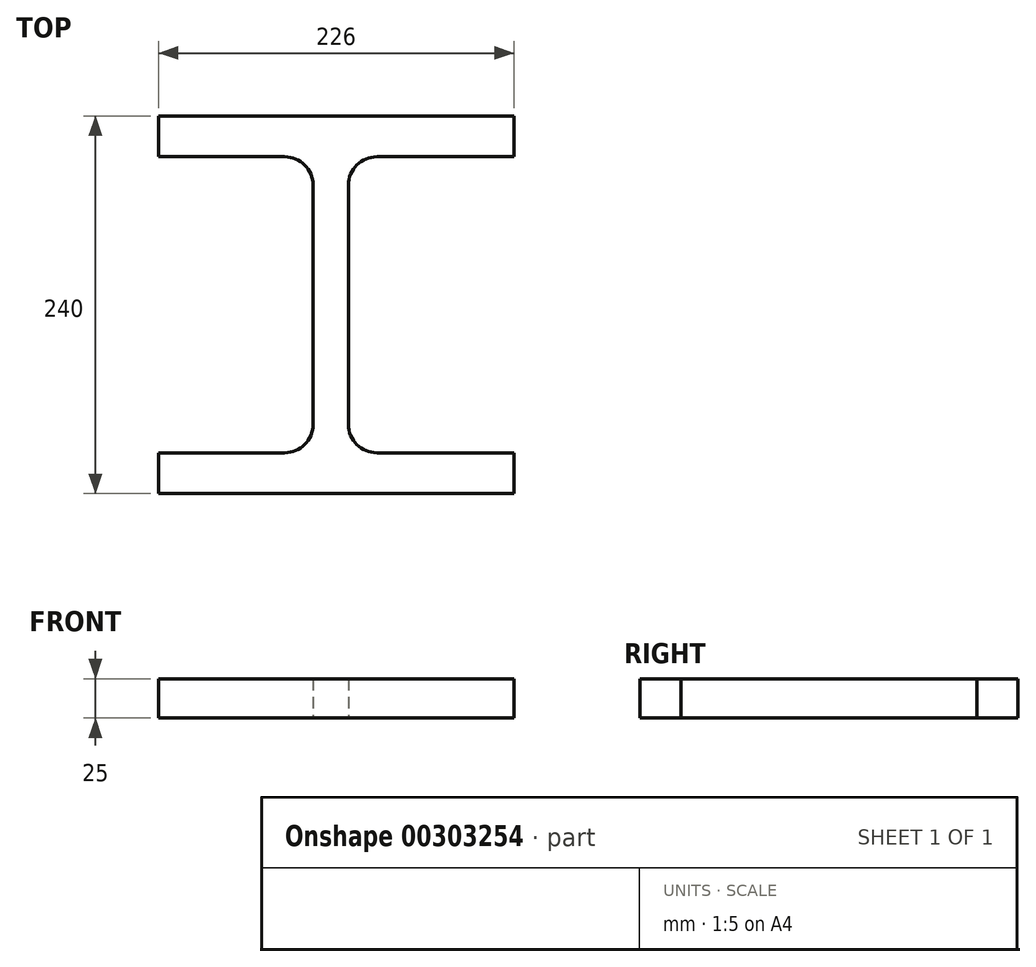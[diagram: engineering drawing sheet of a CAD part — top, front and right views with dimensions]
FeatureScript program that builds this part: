
annotation { "Feature Type Name" : "Feature", "Feature Type Description" : "" }
export const myFeature = defineFeature(function(context is Context, id is Id, definition is map)
    precondition{}
    {
        {
            var Q0;
            Q0=qCreatedBy(makeId("Top.planeOp"),FACE);
            var sketch = newSketch(context, id + "F0", { "sketchPlane" : qUnion([Q0])});
            skLineSegment(sketch, "E0", {"start": v(-54.07, 60.62) * mm, "end": v(-54.07, 34.62) * mm});
            skLineSegment(sketch, "E1", {"start": v(-54.07, 60.62) * mm, "end": v(171.93, 60.62) * mm});
            skLineSegment(sketch, "E2", {"start": v(171.93, 60.62) * mm, "end": v(171.93, 34.62) * mm});
            skLineSegment(sketch, "E3", {"start": v(171.93, 34.62) * mm, "end": v(84.68, 34.62) * mm});
            skLineSegment(sketch, "E4", {"start": v(-54.07, -179.38) * mm, "end": v(171.93, -179.38) * mm});
            skLineSegment(sketch, "E5", {"start": v(-54.07, -179.38) * mm, "end": v(-54.07, -153.38) * mm});
            skLineSegment(sketch, "E6", {"start": v(-54.07, -153.38) * mm, "end": v(26.18, -153.38) * mm});
            skLineSegment(sketch, "E7", {"start": v(171.93, -153.38) * mm, "end": v(171.93, -179.38) * mm});
            skLineSegment(sketch, "E8", {"start": v(44.18, 16.62) * mm, "end": v(44.18, -135.38) * mm});
            skLineSegment(sketch, "E9", {"start": v(66.68, -135.38) * mm, "end": v(66.68, 16.62) * mm});
            skLineSegment(sketch, "E10", {"start": v(171.93, -179.38) * mm, "end": v(171.93, -153.38) * mm});
            skLineSegment(sketch, "E11.trimOffspring", {"start": v(26.18, 34.62) * mm, "end": v(-54.07, 34.62) * mm});
            skLineSegment(sketch, "E12.trimOffspring", {"start": v(84.68, -153.38) * mm, "end": v(171.93, -153.38) * mm});
            skPoint(sketch, "E13.visualSharp", {"position": v(44.18, 34.62) * mm});
            skArc(sketch, "E13.filletArc", {"start": v(44.18, 16.62) * mm, "mid": v(38.91, 29.35) * mm, "end": v(26.18, 34.62) * mm});
            skPoint(sketch, "E14.visualSharp", {"position": v(66.68, 34.62) * mm});
            skArc(sketch, "E14.filletArc", {"start": v(84.68, 34.62) * mm, "mid": v(71.96, 29.35) * mm, "end": v(66.68, 16.62) * mm});
            skPoint(sketch, "E15.visualSharp", {"position": v(44.18, -153.38) * mm});
            skArc(sketch, "E15.filletArc", {"start": v(26.18, -153.38) * mm, "mid": v(38.91, -148.1) * mm, "end": v(44.18, -135.38) * mm});
            skPoint(sketch, "E16.visualSharp", {"position": v(66.68, -153.38) * mm});
            skArc(sketch, "E16.filletArc", {"start": v(66.68, -135.38) * mm, "mid": v(71.96, -148.1) * mm, "end": v(84.68, -153.38) * mm});
            skSolve(sketch);
        }
        {
            var Q0;
            Q0 = qSketchRegion(id + "F0", true);
            extrude(context, id + "F1", {"entities" : qUnion([Q0]), "depth" : 25 * mm});
        }
    });
